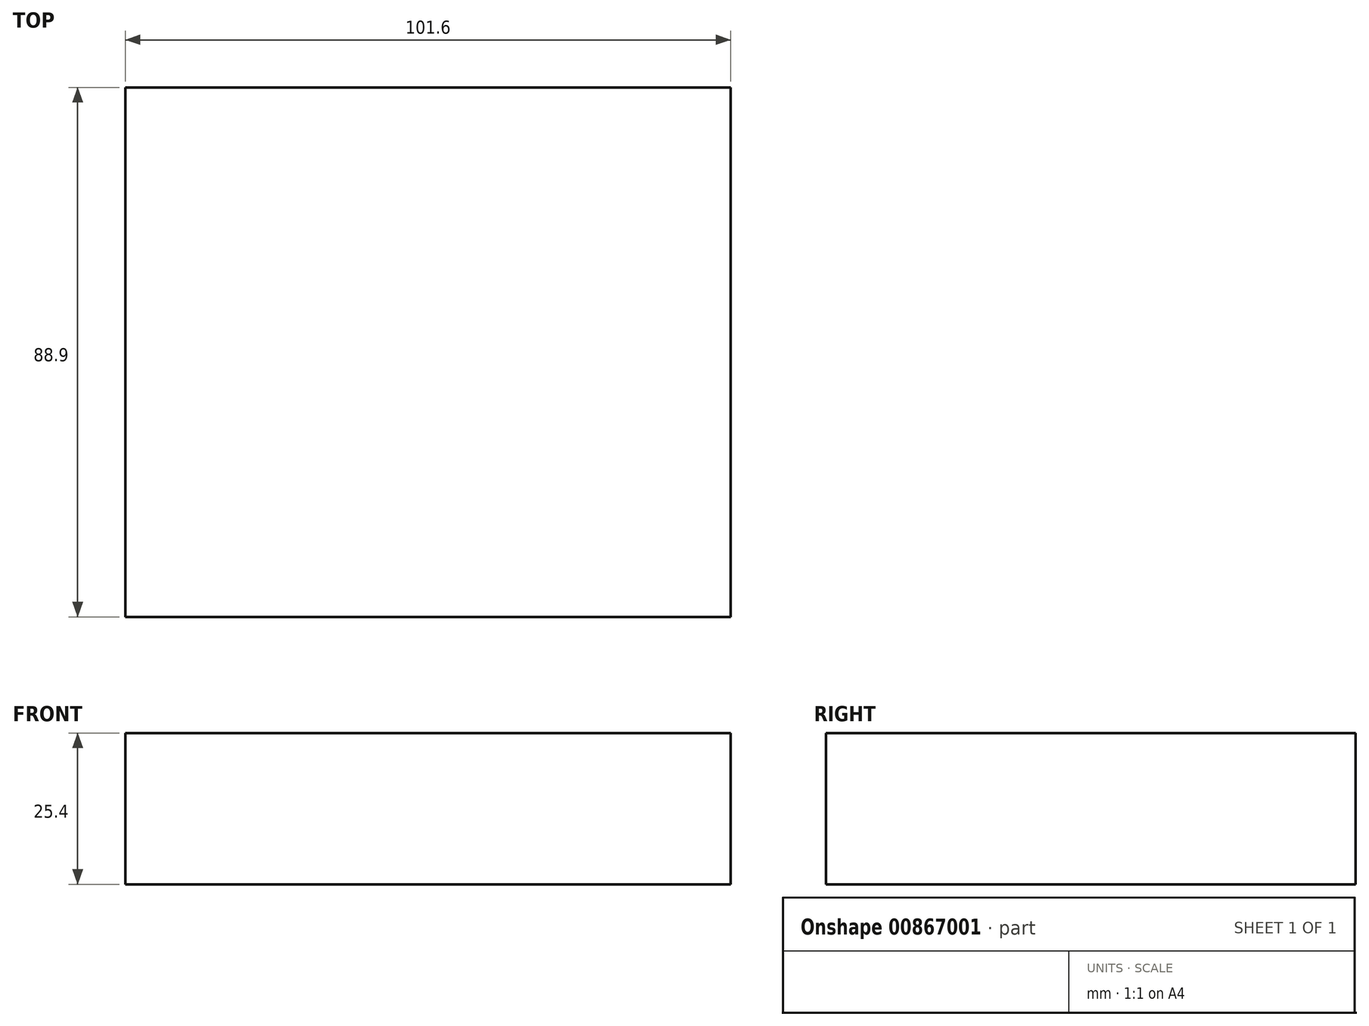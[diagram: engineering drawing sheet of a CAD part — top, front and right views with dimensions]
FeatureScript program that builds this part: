
annotation { "Feature Type Name" : "Feature", "Feature Type Description" : "" }
export const myFeature = defineFeature(function(context is Context, id is Id, definition is map)
    precondition{}
    {
        {
            var Q0;
            Q0=qCreatedBy(makeId("Top.planeOp"),FACE);
            var sketch = newSketch(context, id + "F0", { "sketchPlane" : qUnion([Q0])});
            skLineSegment(sketch, "E0.bottom", {"start": v(50.8, 44.45) * mm, "end": v(-50.8, 44.45) * mm});
            skLineSegment(sketch, "E0.top", {"start": v(50.8, -44.45) * mm, "end": v(-50.8, -44.45) * mm});
            skLineSegment(sketch, "E0.left", {"start": v(50.8, 44.45) * mm, "end": v(50.8, -44.45) * mm});
            skLineSegment(sketch, "E0.right", {"start": v(-50.8, 44.45) * mm, "end": v(-50.8, -44.45) * mm});
            skPoint(sketch, "E0.middle", {"position": v(0, 0) * mm});
            skSolve(sketch);
        }
        {
            var Q0;
            Q0 = qSketchRegion(id + "F0", true);
            extrude(context, id + "F1", {"entities" : qUnion([Q0]), "depth" : 25.4 * mm, "offsetDistance" : 25.4 * mm});
        }
    });
